# Revit family: Kugelhahn mit Kn.griff (ROT) 2201
name_source: partatom
category: Rohrzubehör
units: mm (PartAtom-declared; Revit-internal decimal feet)

## family parameters
Arbeitsebenenbasiert = Nein
Beim Laden mit Abzugskörper schneiden = Nein
Bemaßung runder Anschluss = Durchmesser verwenden
Gemeinsam genutzt = Nein
Immer vertikal = Ja
OmniClass-Nummer = 23.65.55.14
OmniClass-Titel = Valves for Liquid Services
Teiletyp = Unterbricht

## types (2) — shared parameters
Anwendungen = Der Kugelhahn wird in der Installation als Absperreinrichtung verwendet.
Anwendungsgebiete sind Zentralheizungs- und Kälteanlagenlagen.
Die Betriebsbedingungen (wie Temperatur und Druck) sollten dabei eingehalten werden.
Einsatzbereich = Kugelhähne werden zum Absperren von Leitungen und Anlagen verwendet.
Einsatzbereiche sind Heizungs- und Kälteanlagen.
Der Kugelhahn ist nicht geeignet für die Durchflussregelung und muss immer in voll geöffneter oder geschlossener Position verwendet werden.
Gehäuse = geschmiedetes Messing nach EN 12165, vernickelt, CW617N
Griff = verlängerter Knebelgriff rot, Kunststoff PA66 GF30
Hersteller = HERZ Armaturen Ges.m.b.H
Innengewinde = nach ISO 228-1
Kugel = geschmiedetes Messing nach EN 12165, voller Durchgang, verchromt, CW617N
Kugeldichtung = PTFE
Max.Betriebsdruck = 2500000.0 Pa
Max.Betriebsdruck (Verschraubung) = 1600000.0 Pa
Max.Betriebstemperatur = 150 °C
Max.Betriebstemperatur (Wasser - kein Dampf) = 110 °C
Medium = Heizungswasserqualität nach ÖNORM H 5195 oder VDI-Richtline 2035.
Die Verwendung von Ethylen- oder Propylenglykol in einem Mischungsverhältnis 25 - 50% ist zulässig.
Min.Betriebstemperatur = -30 °C
Min.Betriebstemperatur (Wasser) = 1 °C
SCRNCODE = 05;10;02
SCRNSEQ = ARM;ARM_TYP="ABVS";2
Spindel = Messing nach EN 12164, CW614N
Spindeldichtung = PTFE
URL = www.herz-armaturen.at
W01 = 135.00°
zero-valued in all types: Vorgabe-Ansicht

## per-type parameters (varying)
| type | Dämmung |
| Mit Dämmung | Ja |
| Ohne Dämmung | Nein |
